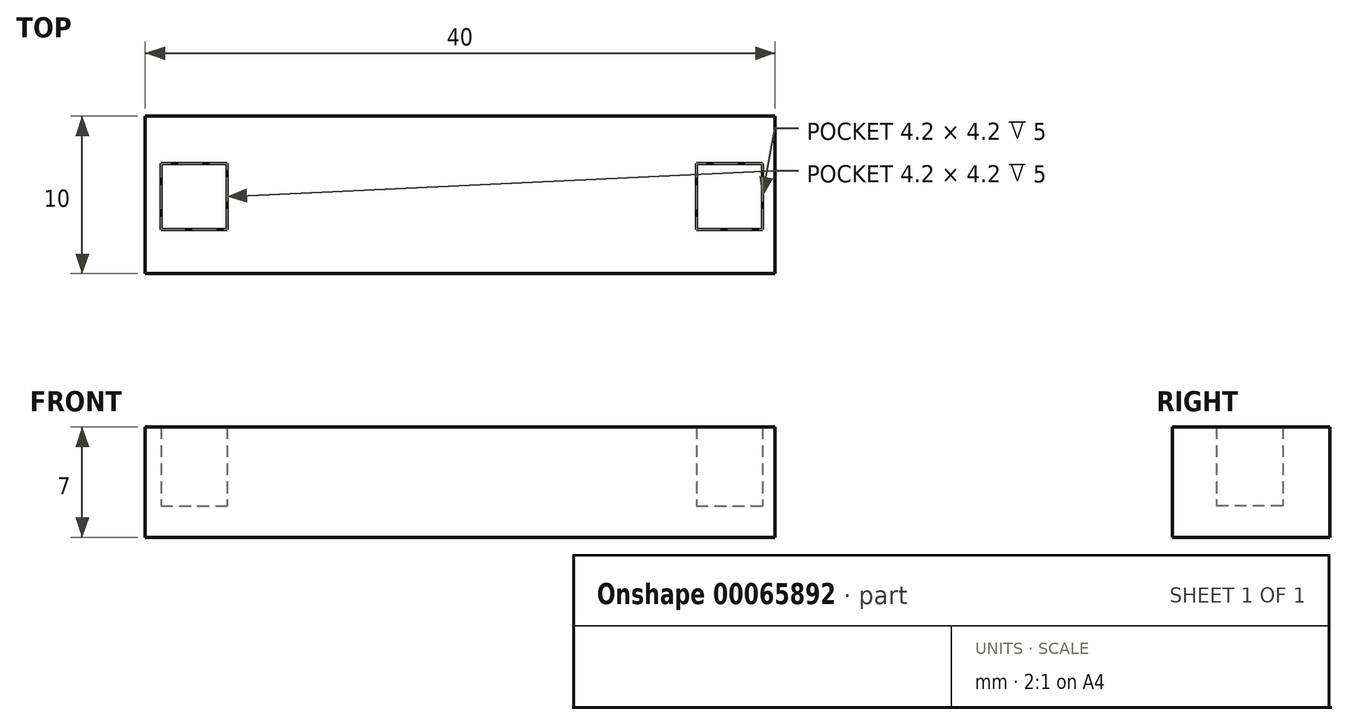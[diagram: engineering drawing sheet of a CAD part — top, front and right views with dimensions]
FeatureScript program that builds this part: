
annotation { "Feature Type Name" : "Feature", "Feature Type Description" : "" }
export const myFeature = defineFeature(function(context is Context, id is Id, definition is map)
    precondition{}
    {
        {
            var Q0;
            Q0=qCreatedBy(makeId("Top.planeOp"),FACE);
            var sketch = newSketch(context, id + "F0", { "sketchPlane" : qUnion([Q0])});
            skLineSegment(sketch, "E0.bottom", {"start": v(-40.84, 22.48) * mm, "end": v(-0.84, 22.48) * mm});
            skLineSegment(sketch, "E0.top", {"start": v(-40.84, 12.48) * mm, "end": v(-0.84, 12.48) * mm});
            skLineSegment(sketch, "E0.left", {"start": v(-40.84, 22.48) * mm, "end": v(-40.84, 12.48) * mm});
            skLineSegment(sketch, "E0.right", {"start": v(-0.84, 22.48) * mm, "end": v(-0.84, 12.48) * mm});
            skSolve(sketch);
        }
        {
            var Q0;
            Q0=makeQuery(id+"F0.imprint","IMPRINT",FACE,{"disambiguationData":[TD([[makeQuery(id+"F0.imprint","IMPRINT",EDGE,{"derivedFrom":sQuery(id+"F0.wireOp",EDGE,"E0.bottom")}),-1.0]])]});
            extrude(context, id + "F1", {"entities" : qUnion([Q0]), "depth" : 2 * mm});
        }
        {
            var Q0;
            Q0=makeQuery(id+"F1.opExtrude","CAP_FACE",FACE,{"disambiguationData":[OSD([sQuery(id+"F0.wireOp",EDGE,"E0.bottom"),sQuery(id+"F0.wireOp",EDGE,"E0.top"),sQuery(id+"F0.wireOp",EDGE,"E0.left"),sQuery(id+"F0.wireOp",EDGE,"E0.right")])],"isStart":false});
            var sketch = newSketch(context, id + "F2", { "sketchPlane" : qUnion([Q0])});
            skLineSegment(sketch, "E1.0.0", {"start": v(-0.84, 22.48) * mm, "end": v(-40.84, 22.48) * mm});
            skLineSegment(sketch, "E1.0.1", {"start": v(-40.84, 22.48) * mm, "end": v(-40.84, 12.48) * mm});
            skLineSegment(sketch, "E1.0.2", {"start": v(-40.84, 12.48) * mm, "end": v(-0.84, 12.48) * mm});
            skLineSegment(sketch, "E1.0.3", {"start": v(-0.84, 12.48) * mm, "end": v(-0.84, 22.48) * mm});
            skLineSegment(sketch, "E2.bottom", {"start": v(-39.84, 19.48) * mm, "end": v(-35.64, 19.48) * mm});
            skLineSegment(sketch, "E2.top", {"start": v(-39.84, 15.28) * mm, "end": v(-35.64, 15.28) * mm});
            skLineSegment(sketch, "E2.left", {"start": v(-39.84, 19.48) * mm, "end": v(-39.84, 15.28) * mm});
            skLineSegment(sketch, "E2.right", {"start": v(-35.64, 19.48) * mm, "end": v(-35.64, 15.28) * mm});
            skLineSegment(sketch, "E3.1.0.0", {"start": v(-5.84, 19.48) * mm, "end": v(-1.64, 19.48) * mm});
            skLineSegment(sketch, "E3.1.0.1", {"start": v(-5.84, 19.48) * mm, "end": v(-5.84, 15.28) * mm});
            skLineSegment(sketch, "E3.1.0.2", {"start": v(-5.84, 15.28) * mm, "end": v(-1.64, 15.28) * mm});
            skLineSegment(sketch, "E3.1.0.3", {"start": v(-1.64, 19.48) * mm, "end": v(-1.64, 15.28) * mm});
            skLineSegment(sketch, "E3.direction1", {"start": v(-39.84, 19.48) * mm, "end": v(-5.84, 19.48) * mm, "construction": true});
            skSolve(sketch);
        }
        {
            var Q0;
            Q0 = qSketchRegion(id + "F2", true);
            extrude(context, id + "F3", {"entities" : qUnion([Q0]), "operationType" : NewBodyOperationType.ADD, "depth" : 5 * mm});
        }
    });
